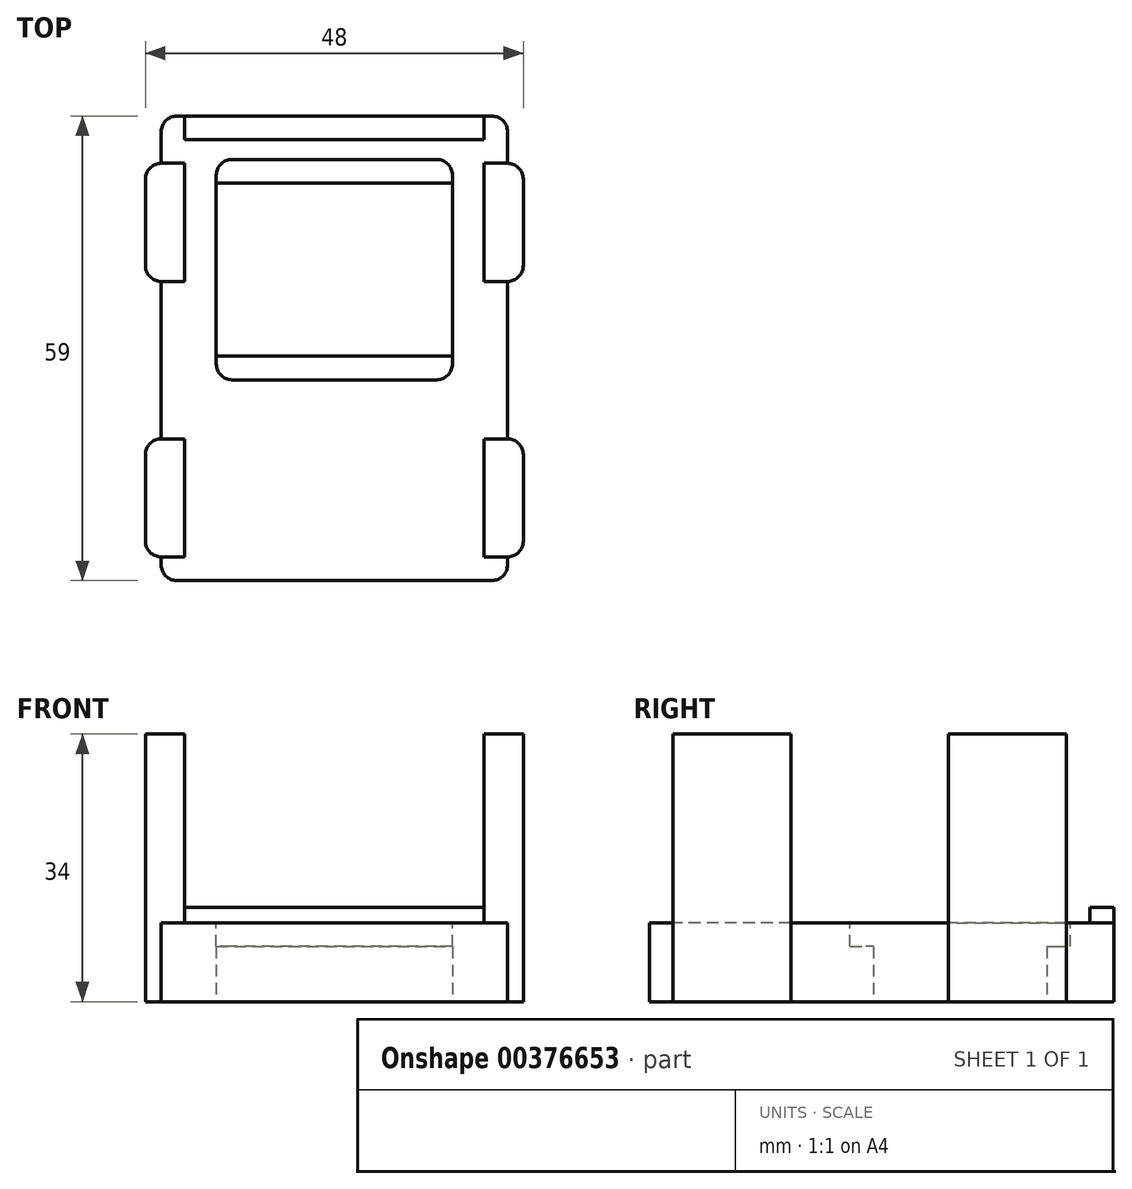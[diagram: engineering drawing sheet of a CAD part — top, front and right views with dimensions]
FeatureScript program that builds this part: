
annotation { "Feature Type Name" : "Feature", "Feature Type Description" : "" }
export const myFeature = defineFeature(function(context is Context, id is Id, definition is map)
    precondition{}
    {
        {
            var Q0;
            Q0=qCreatedBy(makeId("Top.planeOp"),FACE);
            var sketch = newSketch(context, id + "F0", { "sketchPlane" : qUnion([Q0])});
            skLineSegment(sketch, "E0.bottom", {"start": v(-15, -12) * mm, "end": v(15, -12) * mm});
            skLineSegment(sketch, "E0.top", {"start": v(-15, 10) * mm, "end": v(15, 10) * mm});
            skLineSegment(sketch, "E0.left", {"start": v(-15, -12) * mm, "end": v(-15, 10) * mm});
            skLineSegment(sketch, "E0.right", {"start": v(15, -12) * mm, "end": v(15, 10) * mm});
            skPoint(sketch, "E1", {"position": v(0, -11) * mm});
            skLineSegment(sketch, "E2.bottom", {"start": v(22, 18.5) * mm, "end": v(-22, 18.5) * mm});
            skLineSegment(sketch, "E2.top", {"start": v(22, -40.5) * mm, "end": v(-22, -40.5) * mm});
            skLineSegment(sketch, "E2.left", {"start": v(22, 18.5) * mm, "end": v(22, -40.5) * mm});
            skLineSegment(sketch, "E2.right", {"start": v(-22, 18.5) * mm, "end": v(-22, -40.5) * mm});
            skSolve(sketch);
        }
        {
            var Q0;
            Q0=makeQuery(id+"F0.imprint","IMPRINT",FACE,{"disambiguationData":[TD([[makeQuery(id+"F0.imprint","IMPRINT",EDGE,{"derivedFrom":sQuery(id+"F0.wireOp",EDGE,"E0.bottom")}),-1.0]])]});
            extrude(context, id + "F1", {"entities" : qUnion([Q0]), "depth" : 10 * mm});
        }
        {
            var Q0;
            Q0=makeQuery(id+"F1.opExtrude","CAP_FACE",FACE,{"disambiguationData":[OSD([sQuery(id+"F0.wireOp",EDGE,"E0.bottom"),sQuery(id+"F0.wireOp",EDGE,"E0.top"),sQuery(id+"F0.wireOp",EDGE,"E0.left"),sQuery(id+"F0.wireOp",EDGE,"E0.right"),sQuery(id+"F0.wireOp",EDGE,"E2.bottom"),sQuery(id+"F0.wireOp",EDGE,"E2.top"),sQuery(id+"F0.wireOp",EDGE,"E2.left"),sQuery(id+"F0.wireOp",EDGE,"E2.right")])],"isStart":false});
            var sketch = newSketch(context, id + "F2", { "sketchPlane" : qUnion([Q0])});
            skLineSegment(sketch, "E3.bottom", {"start": v(15, 10) * mm, "end": v(-15, 10) * mm});
            skLineSegment(sketch, "E3.top", {"start": v(15, 13) * mm, "end": v(-15, 13) * mm});
            skLineSegment(sketch, "E3.left", {"start": v(15, 10) * mm, "end": v(15, 13) * mm});
            skLineSegment(sketch, "E3.right", {"start": v(-15, 10) * mm, "end": v(-15, 13) * mm});
            skLineSegment(sketch, "E4.bottom", {"start": v(15, -12) * mm, "end": v(-15, -12) * mm});
            skLineSegment(sketch, "E4.top", {"start": v(15, -15) * mm, "end": v(-15, -15) * mm});
            skLineSegment(sketch, "E4.left", {"start": v(15, -12) * mm, "end": v(15, -15) * mm});
            skLineSegment(sketch, "E4.right", {"start": v(-15, -12) * mm, "end": v(-15, -15) * mm});
            skSolve(sketch);
        }
        {
            var Q0;
            Q0=makeQuery(id+"F2.imprint","IMPRINT",FACE,{"disambiguationData":[TD([[makeQuery(id+"F2.imprint","IMPRINT",EDGE,{"derivedFrom":sQuery(id+"F2.wireOp",EDGE,"E4.bottom")}),-1.0]])]});
            var Q1;
            Q1=makeQuery(id+"F2.imprint","IMPRINT",FACE,{"disambiguationData":[TD([[makeQuery(id+"F2.imprint","IMPRINT",EDGE,{"derivedFrom":sQuery(id+"F2.wireOp",EDGE,"E3.bottom")}),1.0]])]});
            extrude(context, id + "F3", {"entities" : qUnion([Q0, Q1]), "operationType" : NewBodyOperationType.REMOVE, "oppositeDirection" : true, "depth" : 3 * mm});
        }
        {
            var Q0;
            Q0=makeQuery(id+"F2.imprint","IMPRINT",FACE,{"disambiguationData":[TD([[makeQuery(id+"F2.imprint","IMPRINT",EDGE,{"derivedFrom":sQuery(id+"F2.wireOp",EDGE,"E3.top")}),-1.0]])]});
            var sketch = newSketch(context, id + "F4", { "sketchPlane" : qUnion([Q0])});
            skLineSegment(sketch, "E5.bottom", {"start": v(-19, 18.5) * mm, "end": v(19, 18.5) * mm});
            skLineSegment(sketch, "E5.top", {"start": v(-19, 15.5) * mm, "end": v(19, 15.5) * mm});
            skLineSegment(sketch, "E5.left", {"start": v(-19, 18.5) * mm, "end": v(-19, 15.5) * mm});
            skLineSegment(sketch, "E5.right", {"start": v(19, 18.5) * mm, "end": v(19, 15.5) * mm});
            skSolve(sketch);
        }
        {
            var Q0;
            Q0=makeQuery(id+"F4.imprint","IMPRINT",FACE,{"disambiguationData":[TD([[makeQuery(id+"F4.imprint","IMPRINT",EDGE,{"derivedFrom":sQuery(id+"F4.wireOp",EDGE,"E5.bottom")}),1.0]])]});
            extrude(context, id + "F5", {"entities" : qUnion([Q0]), "operationType" : NewBodyOperationType.ADD, "depth" : 2 * mm});
        }
        {
            var Q0;
            Q0=makeQuery(id+"F2.imprint","IMPRINT",FACE,{"disambiguationData":[TD([[makeQuery(id+"F2.imprint","IMPRINT",EDGE,{"derivedFrom":sQuery(id+"F2.wireOp",EDGE,"E3.top")}),-1.0]])]});
            var sketch = newSketch(context, id + "F6", { "sketchPlane" : qUnion([Q0])});
            skLineSegment(sketch, "E6.bottom", {"start": v(-22, 12.5) * mm, "end": v(-19, 12.5) * mm});
            skLineSegment(sketch, "E6.top", {"start": v(-22, -2.5) * mm, "end": v(-19, -2.5) * mm});
            skLineSegment(sketch, "E6.right", {"start": v(-19, 12.5) * mm, "end": v(-19, -2.5) * mm});
            skLineSegment(sketch, "E7.bottom", {"start": v(-22, 12.5) * mm, "end": v(-24, 12.5) * mm});
            skLineSegment(sketch, "E7.top", {"start": v(-22, -2.5) * mm, "end": v(-24, -2.5) * mm});
            skLineSegment(sketch, "E7.right", {"start": v(-24, 12.5) * mm, "end": v(-24, -2.5) * mm});
            skLineSegment(sketch, "E8.bottom", {"start": v(-24, -22.5) * mm, "end": v(-19, -22.5) * mm});
            skLineSegment(sketch, "E8.top", {"start": v(-24, -37.5) * mm, "end": v(-19, -37.5) * mm});
            skLineSegment(sketch, "E8.left", {"start": v(-24, -22.5) * mm, "end": v(-24, -37.5) * mm});
            skLineSegment(sketch, "E8.right", {"start": v(-19, -22.5) * mm, "end": v(-19, -37.5) * mm});
            skLineSegment(sketch, "E9.MirrorCS", {"start": v(19, 12.5) * mm, "end": v(19, -2.5) * mm});
            skLineSegment(sketch, "E10.MirrorCS", {"start": v(22, 12.5) * mm, "end": v(19, 12.5) * mm});
            skLineSegment(sketch, "E11.MirrorCS", {"start": v(22, 12.5) * mm, "end": v(24, 12.5) * mm});
            skLineSegment(sketch, "E12.MirrorCS", {"start": v(22, -2.5) * mm, "end": v(24, -2.5) * mm});
            skLineSegment(sketch, "E13.MirrorCS", {"start": v(22, -2.5) * mm, "end": v(19, -2.5) * mm});
            skLineSegment(sketch, "E14.MirrorCS", {"start": v(24, 12.5) * mm, "end": v(24, -2.5) * mm});
            skLineSegment(sketch, "E15.MirrorCS", {"start": v(19, -22.5) * mm, "end": v(19, -37.5) * mm});
            skLineSegment(sketch, "E16.MirrorCS", {"start": v(24, -22.5) * mm, "end": v(24, -37.5) * mm});
            skLineSegment(sketch, "E17.MirrorCS", {"start": v(24, -22.5) * mm, "end": v(19, -22.5) * mm});
            skLineSegment(sketch, "E18.MirrorCS", {"start": v(24, -37.5) * mm, "end": v(19, -37.5) * mm});
            skSolve(sketch);
        }
        {
            var Q0;
            {var subQ0=sQuery(id+"F6.wireOp",EDGE,"E6.bottom");Q0=makeQuery(id+"F6.imprint","IMPRINT",FACE,{"disambiguationData":[TD([[makeQuery(id+"F6.imprint","IMPRINT",EDGE,{"derivedFrom":subQ0}),-1.0]])]});}
            var Q1;
            {var subQ0=sQuery(id+"F6.wireOp",EDGE,"E7.bottom");Q1=makeQuery(id+"F6.imprint","IMPRINT",FACE,{"disambiguationData":[TD([[makeQuery(id+"F6.imprint","IMPRINT",EDGE,{"derivedFrom":subQ0}),1.0]])]});}
            var Q2;
            {var subQ0=sQuery(id+"F6.wireOp",EDGE,"E8.left");Q2=makeQuery(id+"F6.imprint","IMPRINT",FACE,{"disambiguationData":[TD([[makeQuery(id+"F6.imprint","IMPRINT",EDGE,{"derivedFrom":subQ0}),1.0]])]});}
            var Q3;
            {var subQ0=sQuery(id+"F6.wireOp",EDGE,"E8.right");Q3=makeQuery(id+"F6.imprint","IMPRINT",FACE,{"disambiguationData":[TD([[makeQuery(id+"F6.imprint","IMPRINT",EDGE,{"derivedFrom":subQ0}),-1.0]])]});}
            var Q4;
            {var subQ0=sQuery(id+"F6.wireOp",EDGE,"E11.MirrorCS");Q4=makeQuery(id+"F6.imprint","IMPRINT",FACE,{"disambiguationData":[TD([[makeQuery(id+"F6.imprint","IMPRINT",EDGE,{"derivedFrom":subQ0}),-1.0]])]});}
            var Q5;
            {var subQ0=sQuery(id+"F6.wireOp",EDGE,"E16.MirrorCS");Q5=makeQuery(id+"F6.imprint","IMPRINT",FACE,{"disambiguationData":[TD([[makeQuery(id+"F6.imprint","IMPRINT",EDGE,{"derivedFrom":subQ0}),-1.0]])]});}
            var Q6;
            {var subQ0=sQuery(id+"F6.wireOp",EDGE,"E15.MirrorCS");Q6=makeQuery(id+"F6.imprint","IMPRINT",FACE,{"disambiguationData":[TD([[makeQuery(id+"F6.imprint","IMPRINT",EDGE,{"derivedFrom":subQ0}),1.0]])]});}
            var Q7;
            Q7=makeQuery(id+"F6.imprint","IMPRINT",FACE,{"disambiguationData":[TD([[makeQuery(id+"F6.imprint","IMPRINT",EDGE,{"derivedFrom":sQuery(id+"F6.wireOp",EDGE,"E9.MirrorCS")}),1.0]])]});
            extrude(context, id + "F7", {"entities" : qUnion([Q0, Q1, Q2, Q3, Q4, Q5, Q6, Q7]), "operationType" : NewBodyOperationType.ADD, "depth" : 24 * mm});
        }
        {
            var Q0;
            {var subQ0=sQuery(id+"F6.wireOp",EDGE,"E8.left");Q0=makeQuery(id+"F6.imprint","IMPRINT",FACE,{"disambiguationData":[TD([[makeQuery(id+"F6.imprint","IMPRINT",EDGE,{"derivedFrom":subQ0}),1.0]])]});}
            var Q1;
            {var subQ0=sQuery(id+"F6.wireOp",EDGE,"E7.bottom");Q1=makeQuery(id+"F6.imprint","IMPRINT",FACE,{"disambiguationData":[TD([[makeQuery(id+"F6.imprint","IMPRINT",EDGE,{"derivedFrom":subQ0}),1.0]])]});}
            var Q2;
            {var subQ0=sQuery(id+"F6.wireOp",EDGE,"E16.MirrorCS");Q2=makeQuery(id+"F6.imprint","IMPRINT",FACE,{"disambiguationData":[TD([[makeQuery(id+"F6.imprint","IMPRINT",EDGE,{"derivedFrom":subQ0}),-1.0]])]});}
            var Q3;
            {var subQ0=sQuery(id+"F6.wireOp",EDGE,"E11.MirrorCS");Q3=makeQuery(id+"F6.imprint","IMPRINT",FACE,{"disambiguationData":[TD([[makeQuery(id+"F6.imprint","IMPRINT",EDGE,{"derivedFrom":subQ0}),-1.0]])]});}
            var Q4;
            Q4=makeQuery(id+"F1.opExtrude","CAP_FACE",FACE,{"disambiguationData":[OSD([sQuery(id+"F0.wireOp",EDGE,"E0.bottom"),sQuery(id+"F0.wireOp",EDGE,"E0.top"),sQuery(id+"F0.wireOp",EDGE,"E0.left"),sQuery(id+"F0.wireOp",EDGE,"E0.right"),sQuery(id+"F0.wireOp",EDGE,"E2.bottom"),sQuery(id+"F0.wireOp",EDGE,"E2.top"),sQuery(id+"F0.wireOp",EDGE,"E2.left"),sQuery(id+"F0.wireOp",EDGE,"E2.right")])],"isStart":true});
            extrude(context, id + "F8", {"entities" : qUnion([Q0, Q1, Q2, Q3]), "operationType" : NewBodyOperationType.ADD, "endBound" : BoundingType.UP_TO_SURFACE, "oppositeDirection" : true, "endBoundEntityFace" : qUnion([Q4]), "depth" : 25 * mm});
        }
        {
            var Q0;
            {var subQ0=sQuery(id+"F6.wireOp",EDGE,"E14.MirrorCS");var subQ1=sQuery(id+"F6.wireOp",EDGE,"E11.MirrorCS");Q0=makeQuery(id+"F8.boolean.opBoolean","MERGE",EDGE,{"derivedFrom":[makeQuery(id+"F7.opExtrude","SWEPT_EDGE",EDGE,{"disambiguationData":[OSD([subQ1,subQ0])]}),makeQuery(id+"F8.opExtrude","SWEPT_EDGE",EDGE,{"disambiguationData":[OSD([subQ1,subQ0])]})]});}
            var Q1;
            {var subQ0=sQuery(id+"F6.wireOp",EDGE,"E7.right");var subQ1=sQuery(id+"F6.wireOp",EDGE,"E7.bottom");Q1=makeQuery(id+"F8.boolean.opBoolean","MERGE",EDGE,{"derivedFrom":[makeQuery(id+"F7.opExtrude","SWEPT_EDGE",EDGE,{"disambiguationData":[OSD([subQ1,subQ0])]}),makeQuery(id+"F8.opExtrude","SWEPT_EDGE",EDGE,{"disambiguationData":[OSD([subQ1,subQ0])]})]});}
            var Q2;
            {var subQ0=sQuery(id+"F6.wireOp",EDGE,"E7.right");var subQ1=sQuery(id+"F6.wireOp",EDGE,"E7.top");Q2=makeQuery(id+"F8.boolean.opBoolean","MERGE",EDGE,{"derivedFrom":[makeQuery(id+"F7.opExtrude","SWEPT_EDGE",EDGE,{"disambiguationData":[OSD([subQ1,subQ0])]}),makeQuery(id+"F8.opExtrude","SWEPT_EDGE",EDGE,{"disambiguationData":[OSD([subQ1,subQ0])]})]});}
            var Q3;
            {var subQ0=sQuery(id+"F6.wireOp",EDGE,"E8.left");var subQ1=sQuery(id+"F6.wireOp",EDGE,"E8.bottom");Q3=makeQuery(id+"F8.boolean.opBoolean","MERGE",EDGE,{"derivedFrom":[makeQuery(id+"F7.opExtrude","SWEPT_EDGE",EDGE,{"disambiguationData":[OSD([subQ1,subQ0])]}),makeQuery(id+"F8.opExtrude","SWEPT_EDGE",EDGE,{"disambiguationData":[OSD([subQ1,subQ0])]})]});}
            var Q4;
            {var subQ0=sQuery(id+"F6.wireOp",EDGE,"E8.left");var subQ1=sQuery(id+"F6.wireOp",EDGE,"E8.top");Q4=makeQuery(id+"F8.boolean.opBoolean","MERGE",EDGE,{"derivedFrom":[makeQuery(id+"F7.opExtrude","SWEPT_EDGE",EDGE,{"disambiguationData":[OSD([subQ1,subQ0])]}),makeQuery(id+"F8.opExtrude","SWEPT_EDGE",EDGE,{"disambiguationData":[OSD([subQ1,subQ0])]})]});}
            var Q5;
            {var subQ0=sQuery(id+"F6.wireOp",EDGE,"E18.MirrorCS");var subQ1=sQuery(id+"F6.wireOp",EDGE,"E16.MirrorCS");Q5=makeQuery(id+"F8.boolean.opBoolean","MERGE",EDGE,{"derivedFrom":[makeQuery(id+"F7.opExtrude","SWEPT_EDGE",EDGE,{"disambiguationData":[OSD([subQ1,subQ0])]}),makeQuery(id+"F8.opExtrude","SWEPT_EDGE",EDGE,{"disambiguationData":[OSD([subQ1,subQ0])]})]});}
            var Q6;
            {var subQ0=sQuery(id+"F6.wireOp",EDGE,"E17.MirrorCS");var subQ1=sQuery(id+"F6.wireOp",EDGE,"E16.MirrorCS");Q6=makeQuery(id+"F8.boolean.opBoolean","MERGE",EDGE,{"derivedFrom":[makeQuery(id+"F7.opExtrude","SWEPT_EDGE",EDGE,{"disambiguationData":[OSD([subQ1,subQ0])]}),makeQuery(id+"F8.opExtrude","SWEPT_EDGE",EDGE,{"disambiguationData":[OSD([subQ1,subQ0])]})]});}
            var Q7;
            Q7=makeQuery(id+"F1.opExtrude","SWEPT_EDGE",EDGE,{"disambiguationData":[OSD([sQuery(id+"F0.wireOp",EDGE,"E2.top"),sQuery(id+"F0.wireOp",EDGE,"E2.left")])]});
            var Q8;
            Q8=makeQuery(id+"F1.opExtrude","SWEPT_EDGE",EDGE,{"disambiguationData":[OSD([sQuery(id+"F0.wireOp",EDGE,"E2.top"),sQuery(id+"F0.wireOp",EDGE,"E2.right")])]});
            var Q9;
            Q9=makeQuery(id+"F1.opExtrude","SWEPT_EDGE",EDGE,{"disambiguationData":[OSD([sQuery(id+"F0.wireOp",EDGE,"E2.bottom"),sQuery(id+"F0.wireOp",EDGE,"E2.left")])]});
            var Q10;
            Q10=makeQuery(id+"F1.opExtrude","SWEPT_EDGE",EDGE,{"disambiguationData":[OSD([sQuery(id+"F0.wireOp",EDGE,"E2.bottom"),sQuery(id+"F0.wireOp",EDGE,"E2.right")])]});
            var Q11;
            {var subQ0=sQuery(id+"F6.wireOp",EDGE,"E14.MirrorCS");var subQ1=sQuery(id+"F6.wireOp",EDGE,"E12.MirrorCS");Q11=makeQuery(id+"F8.boolean.opBoolean","MERGE",EDGE,{"derivedFrom":[makeQuery(id+"F7.opExtrude","SWEPT_EDGE",EDGE,{"disambiguationData":[OSD([subQ1,subQ0])]}),makeQuery(id+"F8.opExtrude","SWEPT_EDGE",EDGE,{"disambiguationData":[OSD([subQ1,subQ0])]})]});}
            var Q12;
            Q12=makeQuery(id+"F3.boolean.opBoolean","COPY",EDGE,{"derivedFrom":makeQuery(id+"F3.opExtrude","SWEPT_EDGE",EDGE,{"disambiguationData":[OSD([sQuery(id+"F2.wireOp",EDGE,"E3.top"),sQuery(id+"F2.wireOp",EDGE,"E3.right")])]})});
            var Q13;
            Q13=makeQuery(id+"F3.boolean.opBoolean","COPY",EDGE,{"derivedFrom":makeQuery(id+"F3.opExtrude","SWEPT_EDGE",EDGE,{"disambiguationData":[OSD([sQuery(id+"F2.wireOp",EDGE,"E3.top"),sQuery(id+"F2.wireOp",EDGE,"E3.left")])]})});
            var Q14;
            Q14=makeQuery(id+"F3.boolean.opBoolean","COPY",EDGE,{"derivedFrom":makeQuery(id+"F3.opExtrude","SWEPT_EDGE",EDGE,{"disambiguationData":[OSD([sQuery(id+"F2.wireOp",EDGE,"E4.top"),sQuery(id+"F2.wireOp",EDGE,"E4.right")])]})});
            var Q15;
            Q15=makeQuery(id+"F3.boolean.opBoolean","COPY",EDGE,{"derivedFrom":makeQuery(id+"F3.opExtrude","SWEPT_EDGE",EDGE,{"disambiguationData":[OSD([sQuery(id+"F2.wireOp",EDGE,"E4.top"),sQuery(id+"F2.wireOp",EDGE,"E4.left")])]})});
            fillet(context, id + "F9", {"entities" : qUnion([Q0, Q1, Q2, Q3, Q4, Q5, Q6, Q7, Q8, Q9, Q10, Q11, Q12, Q13, Q14, Q15]), "radius" : 2 * mm, "tangentPropagation" : true, "allowEdgeOverflow" : false});
        }
    });
